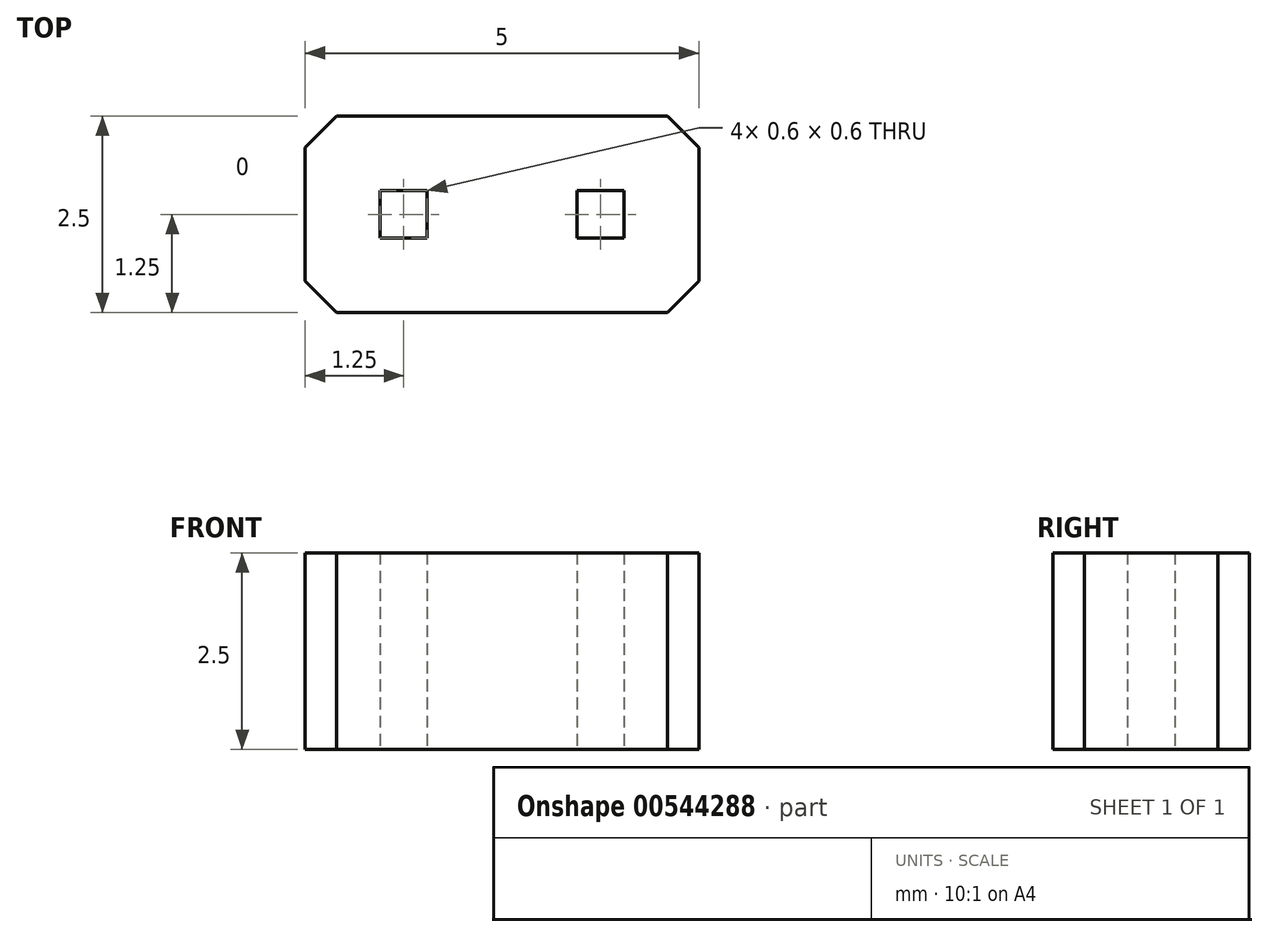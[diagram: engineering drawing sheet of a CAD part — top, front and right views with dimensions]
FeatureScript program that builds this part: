
annotation { "Feature Type Name" : "Feature", "Feature Type Description" : "" }
export const myFeature = defineFeature(function(context is Context, id is Id, definition is map)
    precondition{}
    {
        {
            var Q0;
            Q0=qCreatedBy(makeId("Top.planeOp"),FACE);
            var sketch = newSketch(context, id + "F0", { "sketchPlane" : qUnion([Q0])});
            skLineSegment(sketch, "E0.bottom", {"start": v(0, 2.5) * mm, "end": v(5, 2.5) * mm});
            skLineSegment(sketch, "E0.top", {"start": v(0, 0) * mm, "end": v(5, 0) * mm});
            skLineSegment(sketch, "E0.left", {"start": v(0, 2.5) * mm, "end": v(0, 0) * mm});
            skLineSegment(sketch, "E0.right", {"start": v(5, 2.5) * mm, "end": v(5, 0) * mm});
            skLineSegment(sketch, "E1", {"start": v(2.5, 2.5) * mm, "end": v(2.5, 0) * mm, "construction": true});
            skLineSegment(sketch, "E2.bottom", {"start": v(0.95, 1.55) * mm, "end": v(1.55, 1.55) * mm});
            skLineSegment(sketch, "E2.top", {"start": v(0.95, 0.95) * mm, "end": v(1.55, 0.95) * mm});
            skLineSegment(sketch, "E2.left", {"start": v(0.95, 1.55) * mm, "end": v(0.95, 0.95) * mm});
            skLineSegment(sketch, "E2.right", {"start": v(1.55, 1.55) * mm, "end": v(1.55, 0.95) * mm});
            skLineSegment(sketch, "E3.MirrorCS", {"start": v(3.45, 1.55) * mm, "end": v(3.45, 0.95) * mm});
            skLineSegment(sketch, "E4.MirrorCS", {"start": v(4.05, 1.55) * mm, "end": v(4.05, 0.95) * mm});
            skLineSegment(sketch, "E5.MirrorCS", {"start": v(4.05, 0.95) * mm, "end": v(3.45, 0.95) * mm});
            skLineSegment(sketch, "E6.MirrorCS", {"start": v(4.05, 1.55) * mm, "end": v(3.45, 1.55) * mm});
            skSolve(sketch);
        }
        {
            var Q0;
            Q0=qSketchRegion(id+"F0",true);
            extrude(context, id + "F1", {"entities" : qUnion([Q0]), "depth" : 2.5 * mm});
        }
        {
            var Q0;
            Q0=makeQuery(id+"F1.opExtrude","SWEPT_EDGE",EDGE,{"disambiguationData":[OSD([sQuery(id+"F0.wireOp",EDGE,"E0.bottom"),sQuery(id+"F0.wireOp",EDGE,"E0.left")])]});
            var Q1;
            Q1=makeQuery(id+"F1.opExtrude","SWEPT_EDGE",EDGE,{"disambiguationData":[OSD([sQuery(id+"F0.wireOp",EDGE,"E0.top"),sQuery(id+"F0.wireOp",EDGE,"E0.left")])]});
            var Q2;
            Q2=makeQuery(id+"F1.opExtrude","SWEPT_EDGE",EDGE,{"disambiguationData":[OSD([sQuery(id+"F0.wireOp",EDGE,"E0.top"),sQuery(id+"F0.wireOp",EDGE,"E0.right")])]});
            var Q3;
            Q3=makeQuery(id+"F1.opExtrude","SWEPT_EDGE",EDGE,{"disambiguationData":[OSD([sQuery(id+"F0.wireOp",EDGE,"E0.bottom"),sQuery(id+"F0.wireOp",EDGE,"E0.right")])]});
            chamfer(context, id + "F2", {"entities" : qUnion([Q0, Q1, Q2, Q3]), "width" : 0.4 * mm, "tangentPropagation" : true});
        }
    });
